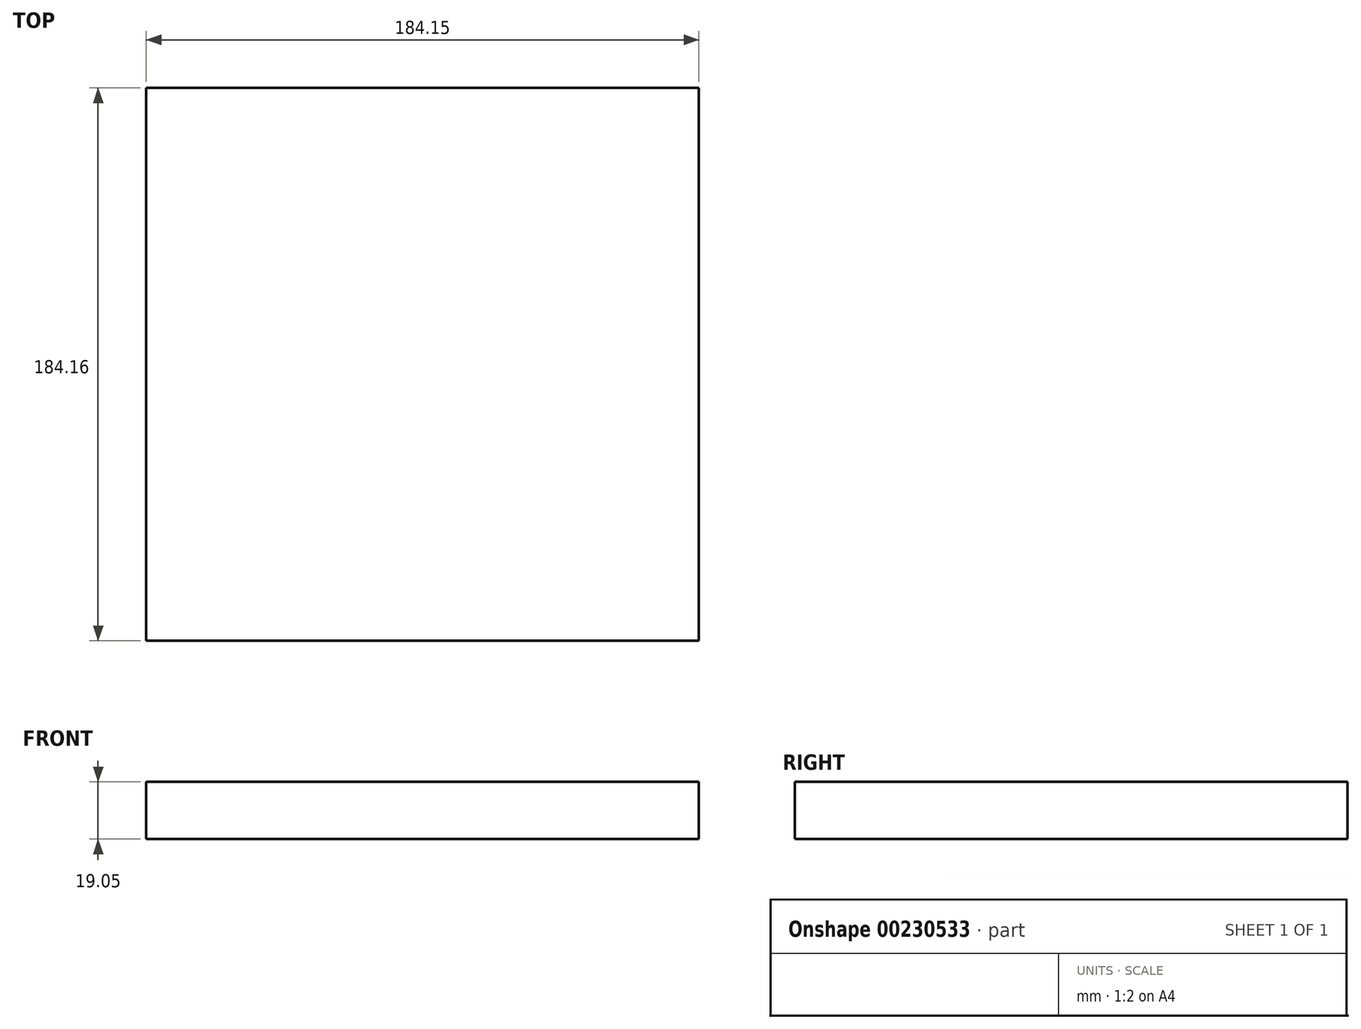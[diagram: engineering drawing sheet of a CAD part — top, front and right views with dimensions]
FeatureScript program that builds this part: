
annotation { "Feature Type Name" : "Feature", "Feature Type Description" : "" }
export const myFeature = defineFeature(function(context is Context, id is Id, definition is map)
    precondition{}
    {
        {
            var Q0;
            Q0=qCreatedBy(makeId("Top.planeOp"),FACE);
            var sketch = newSketch(context, id + "F0", { "sketchPlane" : qUnion([Q0])});
            skLineSegment(sketch, "E0.bottom", {"start": v(94.17, -92.08) * mm, "end": v(-89.98, -92.08) * mm});
            skLineSegment(sketch, "E0.top", {"start": v(94.17, 92.08) * mm, "end": v(-89.98, 92.07) * mm});
            skLineSegment(sketch, "E0.left", {"start": v(94.17, -92.07) * mm, "end": v(94.17, 92.08) * mm});
            skLineSegment(sketch, "E0.right", {"start": v(-89.98, -92.08) * mm, "end": v(-89.98, 92.07) * mm});
            skPoint(sketch, "E0.middle", {"position": v(2.1, 0) * mm});
            skSolve(sketch);
        }
        {
            var Q0;
            Q0=makeQuery(id+"F0.imprint","IMPRINT",FACE,{"disambiguationData":[TD([[makeQuery(id+"F0.imprint","IMPRINT",EDGE,{"derivedFrom":sQuery(id+"F0.wireOp",EDGE,"E0.bottom")}),-1.0]])]});
            extrude(context, id + "F1", {"entities" : qUnion([Q0]), "depth" : 19.05 * mm});
        }
    });
